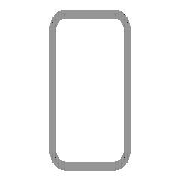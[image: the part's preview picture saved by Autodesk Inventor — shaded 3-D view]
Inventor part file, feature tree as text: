
AUTODESK INVENTOR PART (.ipt)
format: ipt  version: 2025 (Build 290162010, 162A)  size: 136,192 bytes
history: native  units: mm (DEFAULTED — no unit token found)
features: other x4, sketch x1, plane x1
ambient origin geometry x8: Origin, YZ Plane, XZ Plane, XY Plane, X Axis, Y Axis, Z Axis, Center Point
bodies: Solid1 (feature_tree), Body (feature_tree)
feature tree (6):
  parser-record x1  (decoder bookkeeping rows leaked as tree rows — omitted from the tree; the rows remain in map.json)
  other  "Driven Length"
  other  "Start Plane"
  other  "End Plane"
  sketch  "Sketch3"  dims[d3=1420.0mm d4=0.0mm d7=4.0mm d9=40.0mm d11=80.0mm d12=2.0mm d13=40.0mm d14=1460.0mm d15=20.0mm d16=40.0mm d17=90.0deg d18=1420.0mm]
  plane  "Work Plane3"
